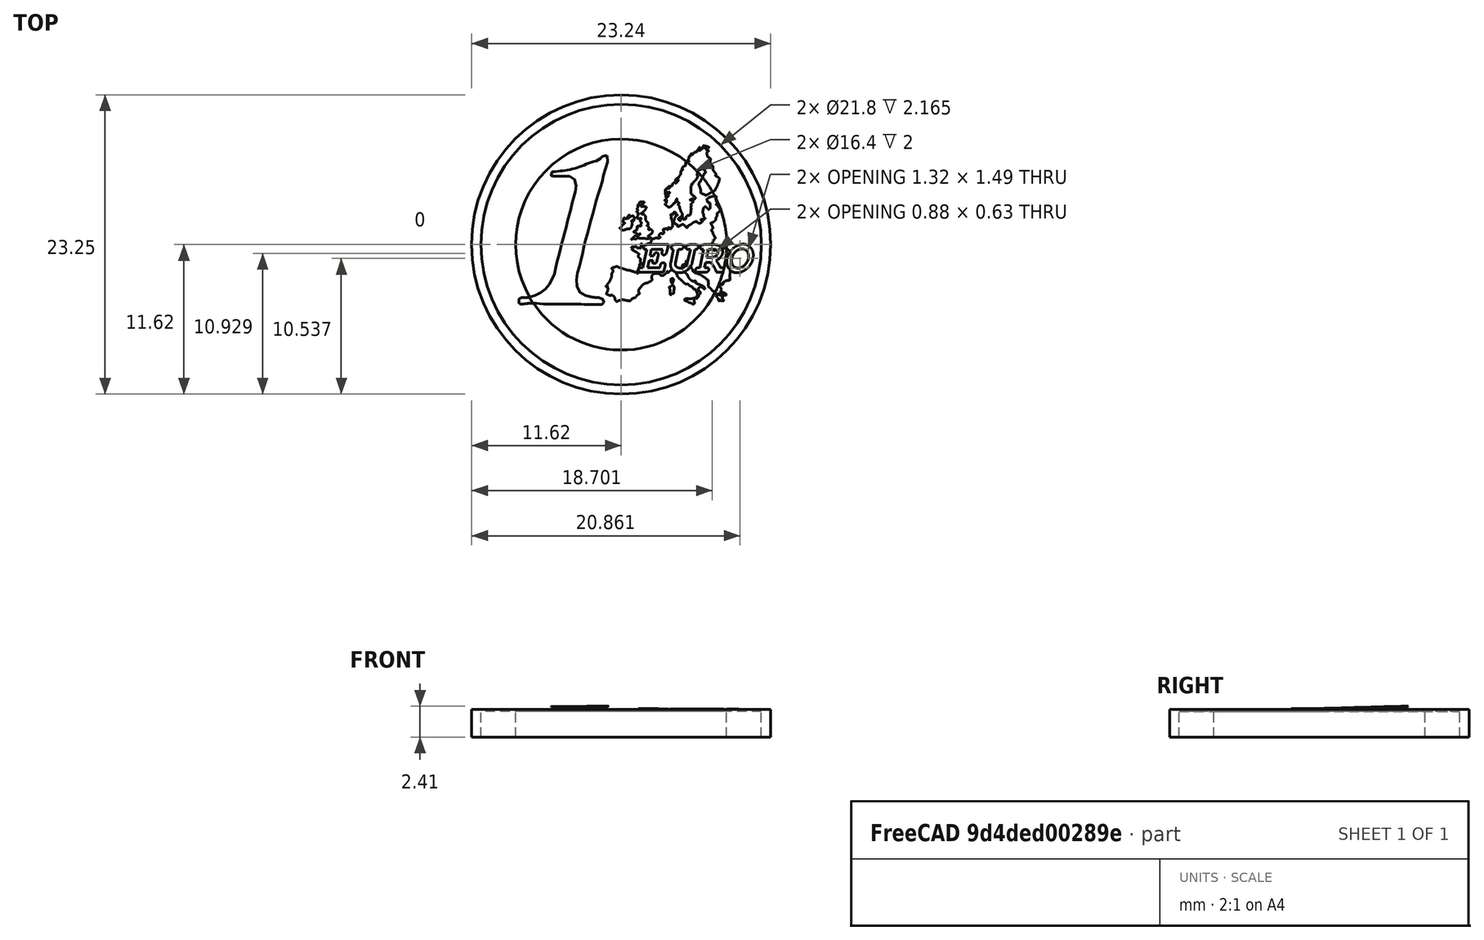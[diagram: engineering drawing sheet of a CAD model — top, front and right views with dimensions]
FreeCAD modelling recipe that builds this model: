
FCSTD DOCUMENT  (FreeCAD 0.15R4671 (Git))
Label: euro-coin
License: CC-BY 3.0
LicenseURL: http://creativecommons.org/licenses/by/3.0/
objects: Part::Extrusion×29, Part::Feature×26, Part::Cylinder×11, Part::MultiFuse×5, Part::Cut×4, Part::MultiCommon×4, App::DocumentObjectGroup×1, Part::Part2DObjectPython×1, Part::Compound×1
note: 81 computed .brp shape members not serialized (recipe doc carries the construction recipe); baked Part::Feature solids carry a one-line shape summary decoded from their .brp

FEATURE [Part::Cylinder] Cylinder  label="Cilindro"
  Angle = 360
  Height = 2.165
  Placement = pos=(0,0.4,-2.33) rot=(0,0,1;0rad)
  Radius = 11.625
FEATURE [Part::Cylinder] Cylinder001  label="Cilindro001"
  Angle = 360
  Height = 2
  Placement = pos=(0,0.4,-2.33) rot=(0,0,1;0rad)
  Radius = 10.9
FEATURE [Part::Cylinder] Cylinder002  label="interior"
  Angle = 360
  Height = 2
  Placement = pos=(0,0.4,0) rot=(0,0,1;0rad)
  Radius = 8.2
FEATURE [Part::Cylinder] Cylinder003  label="Cilindro003"
  Angle = 360
  Height = 2.165
  Placement = pos=(0,0.4,-2.33) rot=(0,0,1;0rad)
  Radius = 10.9
FEATURE [Part::Cut] Cut  label="exterior"
  Base = -> Cylinder
  Placement = pos=(0,0,2.33) rot=(0,0,1;0rad)
  Tool = -> Cylinder003
FEATURE [Part::Cylinder] Cylinder004  label="Cilindro004"
  Angle = 360
  Height = 2
  Placement = pos=(0,0.4,-2.33) rot=(0,0,1;0rad)
  Radius = 8.2
FEATURE [Part::Feature] path3051001
  shape: bbox 11.76 x 7.474 x 2e-07 mm, 0 faces, 0 solids (baked)
FEATURE [Part::Feature] path3051002
  shape: bbox 137.9 x 117 x 2e-07 mm, 0 faces, 0 solids (baked)
FEATURE [Part::Feature] path3051090
  shape: bbox 8.184 x 7.145 x 2e-07 mm, 0 faces, 0 solids (baked)
FEATURE [Part::Feature] path3051092
  shape: bbox 5.679 x 11.23 x 2e-07 mm, 0 faces, 0 solids (baked)
FEATURE [Part::Feature] path3051095
  shape: bbox 3.568 x 6.247 x 2e-07 mm, 0 faces, 0 solids (baked)
FEATURE [Part::Feature] path3051096
  shape: bbox 23.36 x 41.85 x 2e-07 mm, 0 faces, 0 solids (baked)
FEATURE [Part::Feature] path3051098
  shape: bbox 16.3 x 17.05 x 2e-07 mm, 0 faces, 0 solids (baked)
FEATURE [Part::Feature] path3051103
  shape: bbox 3.717 x 5.043 x 2e-07 mm, 0 faces, 0 solids (baked)
FEATURE [Part::Feature] path3051104
  shape: bbox 60.86 x 82.08 x 2e-07 mm, 0 faces, 0 solids (baked)
FEATURE [Part::Feature] Face
  shape: bbox 0.823 x 0.5232 x 2e-07 mm, 1 faces, 0 solids (baked)
FEATURE [Part::Feature] Face001
  shape: bbox 0.3975 x 0.7863 x 2e-07 mm, 1 faces, 0 solids (baked)
FEATURE [Part::Feature] Face002
  shape: bbox 0.5729 x 0.5001 x 2e-07 mm, 1 faces, 0 solids (baked)
FEATURE [Part::Feature] Face003
  shape: bbox 1.141 x 1.194 x 2e-07 mm, 1 faces, 0 solids (baked)
FEATURE [Part::Feature] Face004
  shape: bbox 0.2498 x 0.4373 x 2e-07 mm, 1 faces, 0 solids (baked)
FEATURE [Part::Feature] Face005
  shape: bbox 0.2602 x 0.353 x 2e-07 mm, 1 faces, 0 solids (baked)
FEATURE [Part::Feature] Face006
  shape: bbox 1.635 x 2.93 x 2e-07 mm, 1 faces, 0 solids (baked)
FEATURE [Part::Feature] Face007
  shape: bbox 4.26 x 5.745 x 2e-07 mm, 1 faces, 0 solids (baked)
FEATURE [Part::Feature] Face008
  shape: bbox 9.651 x 8.191 x 2e-07 mm, 1 faces, 0 solids (baked)
FEATURE [Part::Extrusion] Extrude
  Base = -> Face
  Dir = (0,0,0.01)
  Solid = true
FEATURE [Part::Extrusion] Extrude001
  Base = -> Face001
  Dir = (0,0,0.01)
  Solid = true
FEATURE [Part::Extrusion] Extrude002
  Base = -> Face002
  Dir = (0,0,0.01)
  Solid = true
FEATURE [Part::Extrusion] Extrude003
  Base = -> Face003
  Dir = (0,0,0.01)
  Solid = true
FEATURE [Part::Extrusion] Extrude004
  Base = -> Face004
  Dir = (0,0,0.01)
  Solid = true
FEATURE [Part::Extrusion] Extrude005
  Base = -> Face005
  Dir = (0,0,0.01)
  Solid = true
FEATURE [Part::Extrusion] Extrude006
  Base = -> Face006
  Dir = (0,0,0.01)
  Solid = true
FEATURE [Part::Extrusion] Extrude007
  Base = -> Face007
  Dir = (0,0,0.01)
  Solid = true
FEATURE [Part::Extrusion] Extrude008
  Base = -> Face008
  Dir = (0,0,0.01)
  Solid = true
FEATURE [Part::MultiFuse] Fusion
  Shapes = -> [Extrude,Extrude005,Extrude006,Extrude004,Extrude002,Extrude007,Extrude003,Extrude008,Extrude001]
FEATURE [App::DocumentObjectGroup] Grupo  label="map"
  Group = -> [path3051001,path3051002,path3051090,path3051092,path3051095,path3051096,path3051098,path3051103,path3051104,Extrude,Extrude001,Extrude002,Extrude003,Extrude004,Extrude005,Extrude006,Extrude007,Extrude008,Fusion]
FEATURE [Part::Feature] Face009
  shape: bbox 6.969 x 11.59 x 0.3498 mm, 1 faces, 0 solids (baked)
FEATURE [Part::Part2DObjectPython] ShapeString  # Draft 2D object (typed FeaturePython)
  FontFile = <path>
  Placement = pos=(1.3,-1.7,0) rot=(0,0,1;0rad)
  Size = 1.2
  String = EURO
  Tracking = 0
FEATURE [Part::Cut] Cut001  label="middle"
  Base = -> Cylinder001
  Placement = pos=(0,0,2.33) rot=(0,0,1;0rad)
  Tool = -> Cylinder004
FEATURE [Part::Extrusion] Extrude009
  Base = -> Face009
  Dir = (0,0,0.02)
  Solid = true
FEATURE [Part::Extrusion] Extrude010
  Base = -> ShapeString
  Dir = (0,0,0.02)
  Solid = true
FEATURE [Part::MultiFuse] Fusion001  label="text"
  Shapes = -> [Extrude010,Extrude009]
FEATURE [Part::Cylinder] Cylinder005  label="Cilindro005"
  Angle = 360
  Height = 4
  Placement = pos=(0,0.4,-2.33) rot=(0,0,1;0rad)
  Radius = 8.2
FEATURE [Part::MultiFuse] Fusion002  label="text001"
  Shapes = -> [Extrude010,Extrude009]
FEATURE [Part::MultiCommon] Common  label="text-int"
  Placement = pos=(0,-0.0586354,2.19918) rot=(0.164408,0.986296,0.013772;0.005308rad)
  Shapes = -> [Fusion002,Cylinder005]
FEATURE [Part::Cylinder] Cylinder006  label="Cilindro006"
  Angle = 360
  Height = 3
  Placement = pos=(0,0.4,-2.33) rot=(0,0,1;0rad)
  Radius = 10.9
FEATURE [Part::Cylinder] Cylinder007  label="Cilindro007"
  Angle = 360
  Height = 3
  Placement = pos=(0,0.4,-2.33) rot=(0,0,1;0rad)
  Radius = 8.2
FEATURE [Part::Cut] Cut002  label="ext001"
  Base = -> Cylinder006
  Tool = -> Cylinder007
FEATURE [Part::MultiCommon] Common001  label="text-ext"
  Placement = pos=(0,-0.0586354,2.19918) rot=(0.164452,0.986289,0.013772;0.005317rad)
  Shapes = -> [Fusion001,Cut002]
FEATURE [Part::Extrusion] Extrude011
  Base = -> Face008
  Dir = (0,0,0.01)
  Solid = true
FEATURE [Part::Extrusion] Extrude012
  Base = -> Face003
  Dir = (0,0,0.01)
  Solid = true
FEATURE [Part::Extrusion] Extrude013
  Base = -> Face007
  Dir = (0,0,0.01)
  Solid = true
FEATURE [Part::Extrusion] Extrude014
  Base = -> Face002
  Dir = (0,0,0.01)
  Solid = true
FEATURE [Part::Extrusion] Extrude015
  Base = -> Face001
  Dir = (0,0,0.01)
  Solid = true
FEATURE [Part::Extrusion] Extrude016
  Base = -> Face004
  Dir = (0,0,0.01)
  Solid = true
FEATURE [Part::Extrusion] Extrude017
  Base = -> Face006
  Dir = (0,0,0.01)
  Solid = true
FEATURE [Part::Extrusion] Extrude018
  Base = -> Face005
  Dir = (0,0,0.01)
  Solid = true
FEATURE [Part::Extrusion] Extrude019
  Base = -> Face
  Dir = (0,0,0.01)
  Solid = true
FEATURE [Part::MultiFuse] Fusion003
  Shapes = -> [Extrude019,Extrude018,Extrude017,Extrude016,Extrude014,Extrude013,Extrude012,Extrude011,Extrude015]
FEATURE [Part::Cylinder] Cylinder008  label="Cilindro008"
  Angle = 360
  Height = 3
  Placement = pos=(0,0.4,-2.33) rot=(0,0,1;0rad)
  Radius = 8.2
FEATURE [Part::Cylinder] Cylinder009  label="Cilindro009"
  Angle = 360
  Height = 3
  Placement = pos=(0,0.4,-2.33) rot=(0,0,1;0rad)
  Radius = 10.9
FEATURE [Part::Cut] Cut003  label="ext002"
  Base = -> Cylinder009
  Tool = -> Cylinder008
FEATURE [Part::MultiCommon] Common002  label="map-ext"
  Placement = pos=(0,0,2.1) rot=(0,0,1;0rad)
  Shapes = -> [Fusion003,Cut003]
FEATURE [Part::Extrusion] Extrude020
  Base = -> Face008
  Dir = (0,0,0.01)
  Solid = true
FEATURE [Part::Extrusion] Extrude021
  Base = -> Face003
  Dir = (0,0,0.01)
  Solid = true
FEATURE [Part::Extrusion] Extrude022
  Base = -> Face007
  Dir = (0,0,0.01)
  Solid = true
FEATURE [Part::Extrusion] Extrude023
  Base = -> Face002
  Dir = (0,0,0.01)
  Solid = true
FEATURE [Part::Extrusion] Extrude024
  Base = -> Face001
  Dir = (0,0,0.01)
  Solid = true
FEATURE [Part::Extrusion] Extrude025
  Base = -> Face004
  Dir = (0,0,0.01)
  Solid = true
FEATURE [Part::Extrusion] Extrude026
  Base = -> Face006
  Dir = (0,0,0.01)
  Solid = true
FEATURE [Part::Extrusion] Extrude027
  Base = -> Face005
  Dir = (0,0,0.01)
  Solid = true
FEATURE [Part::Extrusion] Extrude028
  Base = -> Face
  Dir = (0,0,0.01)
  Solid = true
FEATURE [Part::MultiFuse] Fusion004
  Shapes = -> [Extrude028,Extrude027,Extrude026,Extrude025,Extrude023,Extrude022,Extrude021,Extrude020,Extrude024]
FEATURE [Part::Cylinder] Cylinder010  label="Cilindro010"
  Angle = 360
  Height = 4
  Placement = pos=(0,0.4,-2.33) rot=(0,0,1;0rad)
  Radius = 8.2
FEATURE [Part::MultiCommon] Common003  label="map-int"
  Placement = pos=(0,0,2.1) rot=(0,0,1;0rad)
  Shapes = -> [Fusion004,Cylinder010]
FEATURE [Part::Feature] Cylinder002001  label="interior001"
  Placement = pos=(0,0.4,0) rot=(0,0,1;0rad)
  shape: bbox 16.4 x 16.4 x 2 mm, 3 faces (baked)
FEATURE [Part::Feature] Cut004  label="exterior001"
  Placement = pos=(0,0,2.33) rot=(0,0,1;0rad)
  shape: bbox 23.25 x 23.25 x 2.165 mm, 4 faces (baked)
FEATURE [Part::Feature] Cut001001  label="middle001"
  Placement = pos=(0,0,2.33) rot=(0,0,1;0rad)
  shape: bbox 21.8 x 21.8 x 2 mm, 4 faces (baked)
FEATURE [Part::Feature] Common004  label="text-int001"
  Placement = pos=(0,-0.0586354,2.19918) rot=(0.164408,0.986296,0.013772;0.005308rad)
  shape: bbox 15.13 x 11.59 x 0.3438 mm, 123 faces, 4 solids (baked)
FEATURE [Part::Feature] Common001001  label="text-ext001"
  Placement = pos=(0,-0.0586354,2.19918) rot=(0.164452,0.986289,0.013772;0.005317rad)
  shape: bbox 18.23 x 4.666 x 0.1049 mm, 26 faces, 2 solids (baked)
FEATURE [Part::Feature] Common002001  label="map-ext001"
  Placement = pos=(0,0,2.1) rot=(0,0,1;0rad)
  shape: bbox 3.332 x 12.09 x 0.01 mm, 138 faces, 4 solids (baked)
FEATURE [Part::Feature] Common003001  label="map-int001"
  Placement = pos=(0,0,2.1) rot=(0,0,1;0rad)
  shape: bbox 9.381 x 11.08 x 0.01 mm, 605 faces, 9 solids (baked)
FEATURE [Part::Compound] Compound  label="Euro-coin-ready"
  Links = -> [Cylinder002001,Common001001,Common003001,Common002001,Common004,Cut004,Cut001001]
note: 1 file-system path scrubbed to <path> (originals preserved in the JSON sidecar)
